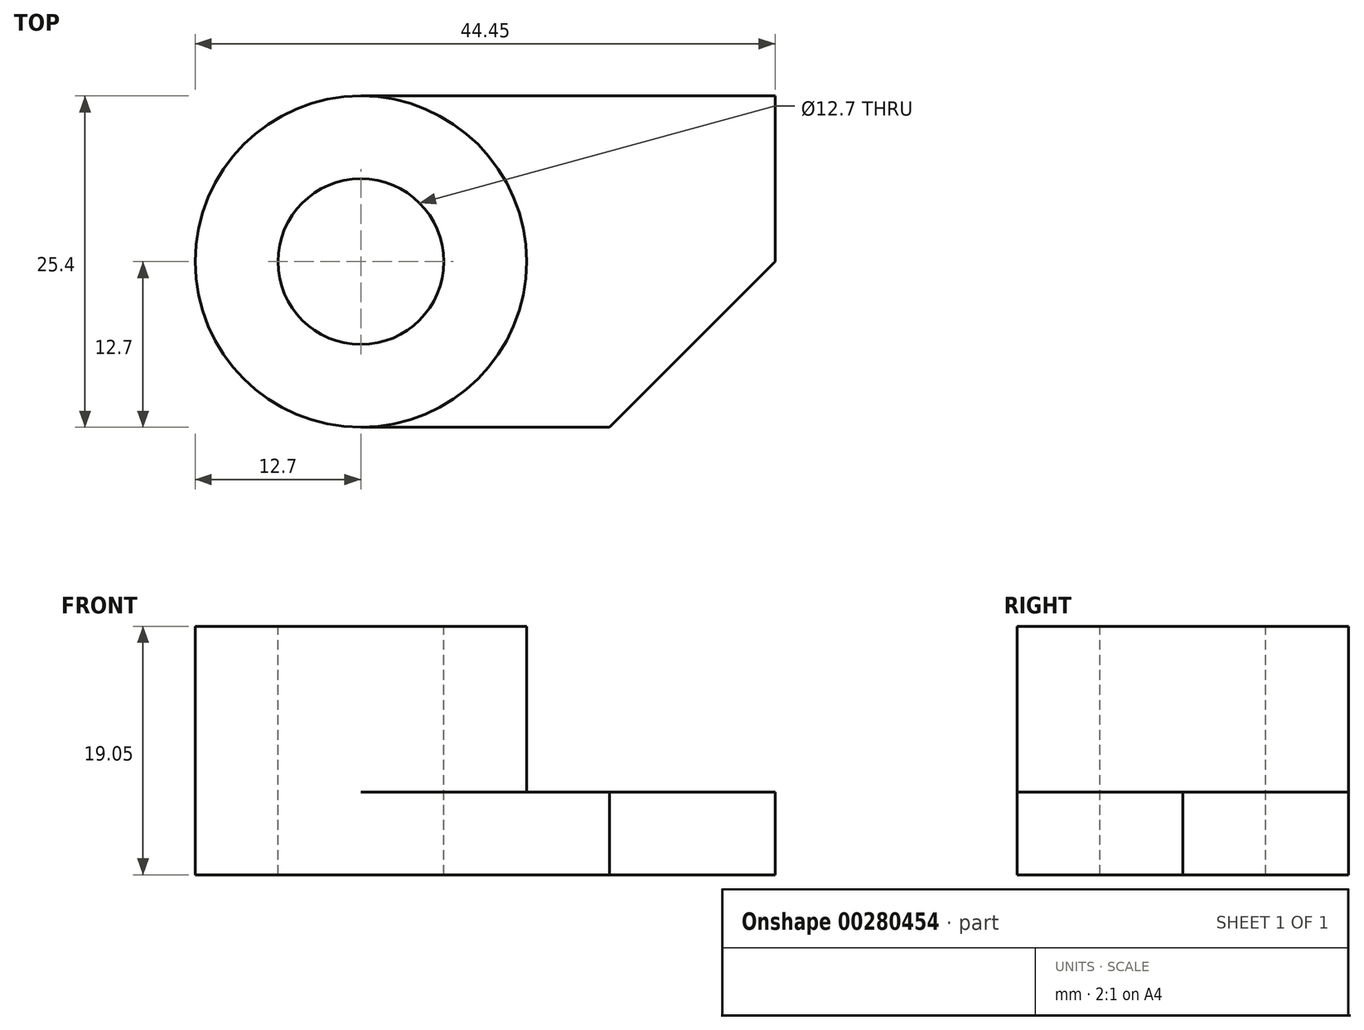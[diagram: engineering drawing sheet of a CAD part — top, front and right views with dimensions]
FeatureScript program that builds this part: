
annotation { "Feature Type Name" : "Feature", "Feature Type Description" : "" }
export const myFeature = defineFeature(function(context is Context, id is Id, definition is map)
    precondition{}
    {
        {
            var Q0;
            Q0=qCreatedBy(makeId("Top.planeOp"),FACE);
            var sketch = newSketch(context, id + "F0", { "sketchPlane" : qUnion([Q0])});
            skLineSegment(sketch, "E0.bottom", {"start": v(0, 0) * mm, "end": v(44.45, 0) * mm});
            skLineSegment(sketch, "E0.top", {"start": v(0, 25.4) * mm, "end": v(44.45, 25.4) * mm});
            skLineSegment(sketch, "E0.left", {"start": v(0, 0) * mm, "end": v(0, 25.4) * mm});
            skLineSegment(sketch, "E0.right", {"start": v(44.45, 0) * mm, "end": v(44.45, 25.4) * mm});
            skSolve(sketch);
        }
        {
            var Q0;
            Q0 = qSketchRegion(id + "F0", true);
            extrude(context, id + "F1", {"entities" : qUnion([Q0]), "depth" : 19.05 * mm});
        }
        {
            var Q0;
            Q0=makeQuery(id+"F1.opExtrude","CAP_FACE",FACE,{"disambiguationData":[OSD([sQuery(id+"F0.wireOp",EDGE,"E0.bottom"),sQuery(id+"F0.wireOp",EDGE,"E0.top"),sQuery(id+"F0.wireOp",EDGE,"E0.left"),sQuery(id+"F0.wireOp",EDGE,"E0.right")])],"isStart":false});
            var sketch = newSketch(context, id + "F2", { "sketchPlane" : qUnion([Q0])});
            skLineSegment(sketch, "E1", {"start": v(44.45, 12.7) * mm, "end": v(31.75, 0) * mm});
            skLineSegment(sketch, "E2", {"start": v(31.75, 0) * mm, "end": v(44.45, 0) * mm});
            skLineSegment(sketch, "E3", {"start": v(44.45, 0) * mm, "end": v(44.45, 12.7) * mm});
            skSolve(sketch);
        }
        {
            var Q0;
            Q0 = qSketchRegion(id + "F2", true);
            extrude(context, id + "F3", {"entities" : qUnion([Q0]), "operationType" : NewBodyOperationType.REMOVE, "endBound" : BoundingType.THROUGH_ALL, "oppositeDirection" : true, "depth" : 25.4 * mm});
        }
        {
            var Q0;
            Q0=makeQuery(id+"F1.opExtrude","CAP_FACE",FACE,{"disambiguationData":[OSD([sQuery(id+"F0.wireOp",EDGE,"E0.bottom"),sQuery(id+"F0.wireOp",EDGE,"E0.top"),sQuery(id+"F0.wireOp",EDGE,"E0.left"),sQuery(id+"F0.wireOp",EDGE,"E0.right")])],"isStart":false});
            var sketch = newSketch(context, id + "F4", { "sketchPlane" : qUnion([Q0])});
            skLineSegment(sketch, "E4", {"start": v(12.7, 0) * mm, "end": v(31.75, 0) * mm});
            skLineSegment(sketch, "E5", {"start": v(31.75, 0) * mm, "end": v(44.45, 12.7) * mm});
            skLineSegment(sketch, "E6", {"start": v(44.45, 12.7) * mm, "end": v(44.45, 25.4) * mm});
            skLineSegment(sketch, "E7", {"start": v(44.45, 25.4) * mm, "end": v(12.7, 25.4) * mm});
            skLineSegment(sketch, "E8", {"start": v(12.7, 25.4) * mm, "end": v(12.7, 0) * mm});
            skSolve(sketch);
        }
        {
            var Q0;
            Q0 = qSketchRegion(id + "F4", true);
            extrude(context, id + "F5", {"entities" : qUnion([Q0]), "operationType" : NewBodyOperationType.REMOVE, "oppositeDirection" : true, "depth" : 12.7 * mm});
        }
        {
            var Q0;
            Q0=makeQuery(id+"F1.opExtrude","CAP_FACE",FACE,{"disambiguationData":[OSD([sQuery(id+"F0.wireOp",EDGE,"E0.bottom"),sQuery(id+"F0.wireOp",EDGE,"E0.top"),sQuery(id+"F0.wireOp",EDGE,"E0.left"),sQuery(id+"F0.wireOp",EDGE,"E0.right")])],"isStart":false});
            var sketch = newSketch(context, id + "F6", { "sketchPlane" : qUnion([Q0])});
            skLineSegment(sketch, "E9.bottom", {"start": v(12.7, 0) * mm, "end": v(0, 0) * mm});
            skLineSegment(sketch, "E9.top", {"start": v(12.7, 25.4) * mm, "end": v(0, 25.4) * mm});
            skLineSegment(sketch, "E9.left", {"start": v(12.7, 0) * mm, "end": v(12.7, 25.4) * mm});
            skLineSegment(sketch, "E9.right", {"start": v(0, 0) * mm, "end": v(0, 25.4) * mm});
            skSolve(sketch);
        }
        {
            var Q0;
            Q0 = qSketchRegion(id + "F6", true);
            extrude(context, id + "F7", {"entities" : qUnion([Q0]), "operationType" : NewBodyOperationType.REMOVE, "oppositeDirection" : true, "depth" : 12.7 * mm});
        }
        {
            var Q0;
            Q0=makeQuery(id+"F7.boolean.opBoolean","MERGE",FACE,{"derivedFrom":[makeQuery(id+"F5.boolean.opBoolean","COPY",FACE,{"derivedFrom":makeQuery(id+"F5.opExtrude","CAP_FACE",FACE,{"disambiguationData":[OSD([sQuery(id+"F4.wireOp",EDGE,"E4"),sQuery(id+"F4.wireOp",EDGE,"E5"),sQuery(id+"F4.wireOp",EDGE,"E6"),sQuery(id+"F4.wireOp",EDGE,"E7"),sQuery(id+"F4.wireOp",EDGE,"E8")])],"isStart":false})}),makeQuery(id+"F7.opExtrude","CAP_FACE",FACE,{"disambiguationData":[OSD([sQuery(id+"F6.wireOp",EDGE,"E9.bottom"),sQuery(id+"F6.wireOp",EDGE,"E9.top"),sQuery(id+"F6.wireOp",EDGE,"E9.left"),sQuery(id+"F6.wireOp",EDGE,"E9.right")])],"isStart":false})]});
            var sketch = newSketch(context, id + "F8", { "sketchPlane" : qUnion([Q0])});
            skCircle(sketch, "E10", {"center": v(12.7, 12.7) * mm, "radius": 12.7 * mm});
            skLineSegment(sketch, "E11", {"start": v(31.75, 0) * mm, "end": v(12.7, 0) * mm});
            skSolve(sketch);
        }
        {
            var Q0;
            Q0 = qSketchRegion(id + "F8", true);
            extrude(context, id + "F9", {"entities" : qUnion([Q0]), "operationType" : NewBodyOperationType.ADD, "depth" : 12.7 * mm, "hasSecondDirection" : true, "secondDirectionOppositeDirection" : true, "secondDirectionDepth" : 6.35 * mm});
        }
        {
            var Q0;
            {var subQ0=makeQuery(id+"F7.opExtrude","CAP_FACE",FACE,{"disambiguationData":[OSD([sQuery(id+"F6.wireOp",EDGE,"E9.bottom"),sQuery(id+"F6.wireOp",EDGE,"E9.top"),sQuery(id+"F6.wireOp",EDGE,"E9.left"),sQuery(id+"F6.wireOp",EDGE,"E9.right")])],"isStart":false});var subQ1=makeQuery(id+"F5.boolean.opBoolean","COPY",FACE,{"derivedFrom":makeQuery(id+"F5.opExtrude","CAP_FACE",FACE,{"disambiguationData":[OSD([sQuery(id+"F4.wireOp",EDGE,"E4"),sQuery(id+"F4.wireOp",EDGE,"E5"),sQuery(id+"F4.wireOp",EDGE,"E6"),sQuery(id+"F4.wireOp",EDGE,"E7"),sQuery(id+"F4.wireOp",EDGE,"E8")])],"isStart":false})});Q0=makeQuery(id+"F9.boolean.opBoolean","SPLIT",FACE,{"disambiguationData":[TD([makeQuery(id+"F1.opExtrude","SWEPT_FACE",FACE,{"disambiguationData":[OSD([sQuery(id+"F0.wireOp",EDGE,"E0.bottom")])]}),makeQuery(id+"F1.opExtrude","SWEPT_FACE",FACE,{"disambiguationData":[OSD([sQuery(id+"F0.wireOp",EDGE,"E0.left")])]}),subQ1,subQ0,makeQuery(id+"F9.opExtrude","SWEPT_FACE",FACE,{"disambiguationData":[OSD([sQuery(id+"F8.wireOp",EDGE,"E10")])]})])],"derivedFrom":makeQuery(id+"F7.boolean.opBoolean","MERGE",FACE,{"derivedFrom":[subQ1,subQ0]})});}
            var sketch = newSketch(context, id + "F10", { "sketchPlane" : qUnion([Q0])});
            skLineSegment(sketch, "E12", {"start": v(0, 0) * mm, "end": v(0, 12.7) * mm});
            skLineSegment(sketch, "E13", {"start": v(12.7, 0) * mm, "end": v(0, 0) * mm});
            skArc(sketch, "E14", {"start": v(0, 12.7) * mm, "mid": v(3.72, 3.72) * mm, "end": v(12.7, 0) * mm});
            skSolve(sketch);
        }
        {
            var Q0;
            Q0 = qSketchRegion(id + "F10", true);
            extrude(context, id + "F11", {"entities" : qUnion([Q0]), "operationType" : NewBodyOperationType.REMOVE, "endBound" : BoundingType.THROUGH_ALL, "oppositeDirection" : true, "depth" : 25.4 * mm});
        }
        {
            var Q0;
            {var subQ0=makeQuery(id+"F7.opExtrude","CAP_FACE",FACE,{"disambiguationData":[OSD([sQuery(id+"F6.wireOp",EDGE,"E9.bottom"),sQuery(id+"F6.wireOp",EDGE,"E9.top"),sQuery(id+"F6.wireOp",EDGE,"E9.left"),sQuery(id+"F6.wireOp",EDGE,"E9.right")])],"isStart":false});var subQ1=makeQuery(id+"F5.boolean.opBoolean","COPY",FACE,{"derivedFrom":makeQuery(id+"F5.opExtrude","CAP_FACE",FACE,{"disambiguationData":[OSD([sQuery(id+"F4.wireOp",EDGE,"E4"),sQuery(id+"F4.wireOp",EDGE,"E5"),sQuery(id+"F4.wireOp",EDGE,"E6"),sQuery(id+"F4.wireOp",EDGE,"E7"),sQuery(id+"F4.wireOp",EDGE,"E8")])],"isStart":false})});Q0=makeQuery(id+"F9.boolean.opBoolean","SPLIT",FACE,{"disambiguationData":[TD([makeQuery(id+"F1.opExtrude","SWEPT_FACE",FACE,{"disambiguationData":[OSD([sQuery(id+"F0.wireOp",EDGE,"E0.top")])]}),makeQuery(id+"F1.opExtrude","SWEPT_FACE",FACE,{"disambiguationData":[OSD([sQuery(id+"F0.wireOp",EDGE,"E0.left")])]}),subQ1,subQ0,makeQuery(id+"F9.opExtrude","SWEPT_FACE",FACE,{"disambiguationData":[OSD([sQuery(id+"F8.wireOp",EDGE,"E10")])]})])],"derivedFrom":makeQuery(id+"F7.boolean.opBoolean","MERGE",FACE,{"derivedFrom":[subQ1,subQ0]})});}
            var sketch = newSketch(context, id + "F12", { "sketchPlane" : qUnion([Q0])});
            skLineSegment(sketch, "E15", {"start": v(0, 12.7) * mm, "end": v(0, 25.4) * mm});
            skLineSegment(sketch, "E16", {"start": v(0, 25.4) * mm, "end": v(12.7, 25.4) * mm});
            skArc(sketch, "E17", {"start": v(12.7, 25.4) * mm, "mid": v(3.72, 21.68) * mm, "end": v(0, 12.7) * mm});
            skSolve(sketch);
        }
        {
            var Q0;
            Q0 = qSketchRegion(id + "F12", true);
            extrude(context, id + "F13", {"entities" : qUnion([Q0]), "operationType" : NewBodyOperationType.REMOVE, "endBound" : BoundingType.THROUGH_ALL, "oppositeDirection" : true, "depth" : 25.4 * mm});
        }
        {
            var Q0;
            Q0=makeQuery(id+"F9.opExtrude","CAP_FACE",FACE,{"disambiguationData":[OSD([sQuery(id+"F8.wireOp",EDGE,"E10")])],"isStart":false});
            var sketch = newSketch(context, id + "F14", { "sketchPlane" : qUnion([Q0])});
            skCircle(sketch, "E18", {"center": v(12.7, 12.7) * mm, "radius": 6.35 * mm});
            skSolve(sketch);
        }
        {
            var Q0;
            Q0 = qSketchRegion(id + "F14", true);
            extrude(context, id + "F15", {"entities" : qUnion([Q0]), "operationType" : NewBodyOperationType.REMOVE, "endBound" : BoundingType.THROUGH_ALL, "oppositeDirection" : true, "depth" : 25.4 * mm});
        }
    });
